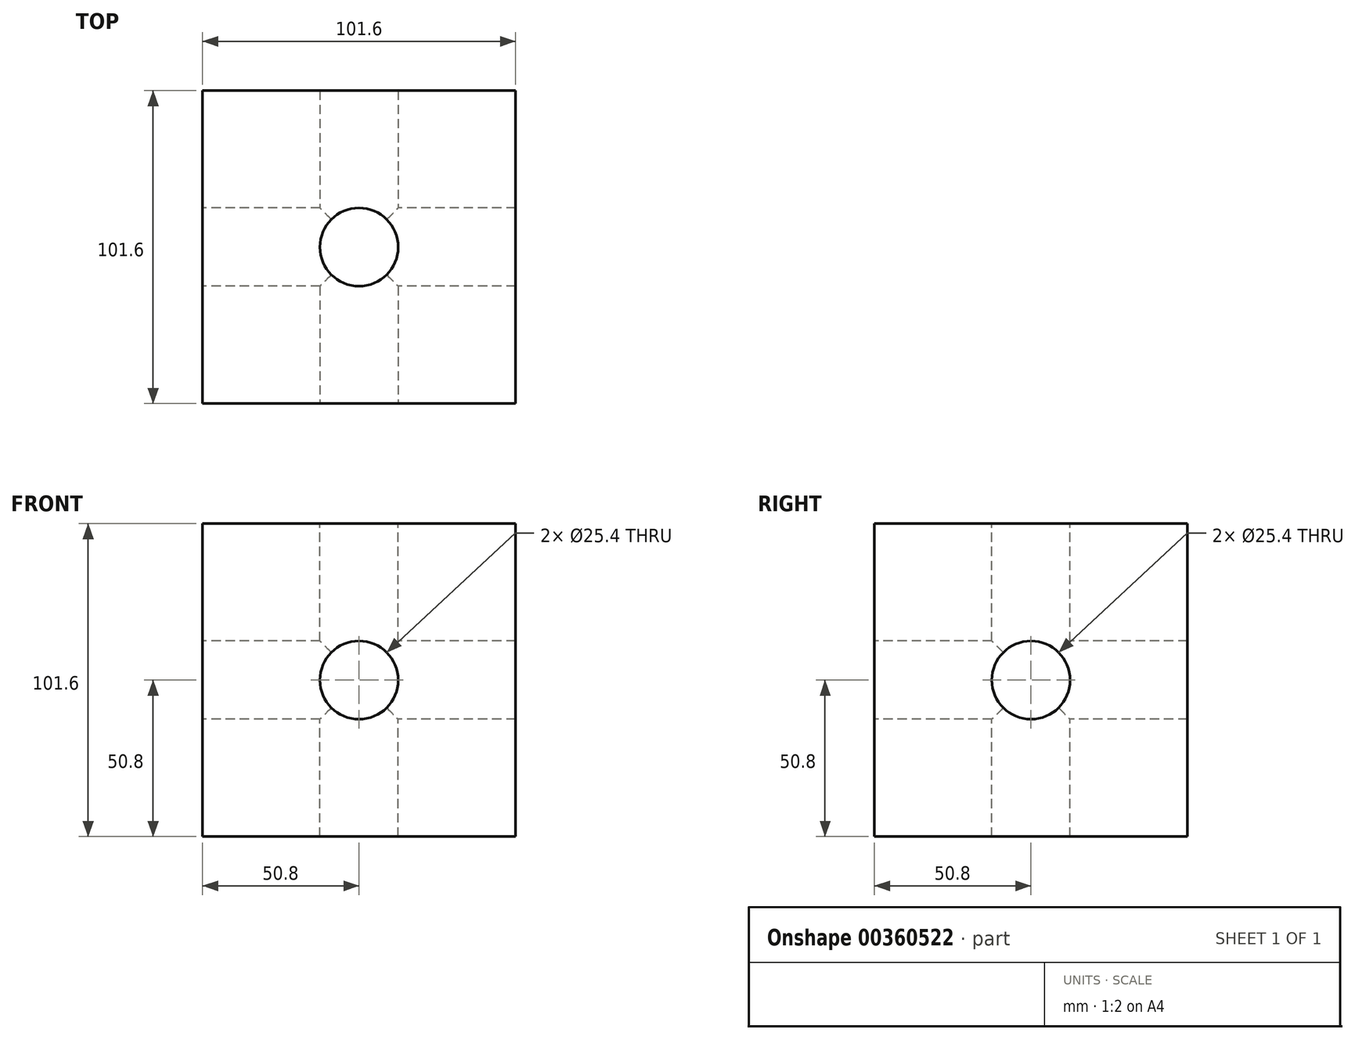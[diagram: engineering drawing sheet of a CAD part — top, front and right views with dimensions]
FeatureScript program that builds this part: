
annotation { "Feature Type Name" : "Feature", "Feature Type Description" : "" }
export const myFeature = defineFeature(function(context is Context, id is Id, definition is map)
    precondition{}
    {
        {
            var Q0;
            Q0=qCreatedBy(makeId("Front.planeOp"),FACE);
            var sketch = newSketch(context, id + "F0", { "sketchPlane" : qUnion([Q0])});
            skLineSegment(sketch, "E0.bottom", {"start": v(0, 0) * mm, "end": v(-50.8, 0) * mm});
            skLineSegment(sketch, "E0.top", {"start": v(0, 50.8) * mm, "end": v(-50.8, 50.8) * mm});
            skLineSegment(sketch, "E0.left", {"start": v(0, 0) * mm, "end": v(0, 50.8) * mm});
            skLineSegment(sketch, "E0.right", {"start": v(-50.8, 0) * mm, "end": v(-50.8, 50.8) * mm});
            skSolve(sketch);
        }
        {
            var Q0;
            Q0 = qSketchRegion(id + "F0", true);
            extrude(context, id + "F1", {"entities" : qUnion([Q0]), "depth" : 50.8 * mm});
        }
        {
            var Q0;
            Q0=qCreatedBy(makeId("Front.planeOp"),FACE);
            var sketch = newSketch(context, id + "F2", { "sketchPlane" : qUnion([Q0])});
            skLineSegment(sketch, "E1.bottom", {"start": v(25.4, -25.4) * mm, "end": v(-76.2, -25.4) * mm});
            skLineSegment(sketch, "E1.top", {"start": v(25.4, 76.2) * mm, "end": v(-76.2, 76.2) * mm});
            skLineSegment(sketch, "E1.left", {"start": v(25.4, -25.4) * mm, "end": v(25.4, 76.2) * mm});
            skLineSegment(sketch, "E1.right", {"start": v(-76.2, -25.4) * mm, "end": v(-76.2, 76.2) * mm});
            skSolve(sketch);
        }
        {
            var Q0;
            Q0=makeQuery(id+"F2.imprint","IMPRINT",FACE,{"disambiguationData":[TD([[makeQuery(id+"F2.imprint","IMPRINT",EDGE,{"derivedFrom":sQuery(id+"F2.wireOp",EDGE,"E1.bottom")}),-1.0]])]});
            extrude(context, id + "F3", {"entities" : qUnion([Q0]), "operationType" : NewBodyOperationType.ADD, "depth" : 76.2 * mm});
        }
        {
            var Q0;
            Q0=makeQuery(id+"F3.boolean.opBoolean","MERGE",FACE,{"derivedFrom":[makeQuery(id+"F1.opExtrude","CAP_FACE",FACE,{"disambiguationData":[OSD([sQuery(id+"F0.wireOp",EDGE,"E0.bottom"),sQuery(id+"F0.wireOp",EDGE,"E0.top"),sQuery(id+"F0.wireOp",EDGE,"E0.left"),sQuery(id+"F0.wireOp",EDGE,"E0.right")])],"isStart":true}),makeQuery(id+"F3.opExtrude","CAP_FACE",FACE,{"disambiguationData":[OSD([sQuery(id+"F2.wireOp",EDGE,"E1.bottom"),sQuery(id+"F2.wireOp",EDGE,"E1.top"),sQuery(id+"F2.wireOp",EDGE,"E1.left"),sQuery(id+"F2.wireOp",EDGE,"E1.right")])],"isStart":true})]});
            extrude(context, id + "F4", {"entities" : qUnion([Q0]), "operationType" : NewBodyOperationType.ADD, "depth" : 25.4 * mm});
        }
        {
            var Q0;
            {var subQ0=sQuery(id+"F2.wireOp",EDGE,"E1.top");Q0=makeQuery(id+"F4.boolean.opBoolean","MERGE",FACE,{"derivedFrom":[makeQuery(id+"F3.opExtrude","SWEPT_FACE",FACE,{"disambiguationData":[OSD([subQ0])]}),makeQuery(id+"F4.opExtrude","SWEPT_FACE",FACE,{"disambiguationData":[OSD([subQ0])]})]});}
            var sketch = newSketch(context, id + "F5", { "sketchPlane" : qUnion([Q0])});
            skCircle(sketch, "E2", {"center": v(-25.4, -25.4) * mm, "radius": 18.47 * mm});
            skSolve(sketch);
        }
        {
            var Q0;
            Q0=sQuery(id+"F5.wireOp",VERTEX,"E2.center");
            var Q1;
            Q1=makeQuery(id+"F1.opExtrude","SWEPT_BODY",BODY,{"disambiguationData":[OSD([sQuery(id+"F0.wireOp",EDGE,"E0.bottom"),sQuery(id+"F0.wireOp",EDGE,"E0.top"),sQuery(id+"F0.wireOp",EDGE,"E0.left"),sQuery(id+"F0.wireOp",EDGE,"E0.right")])]});
            hole(context, id + "F6", {"style" : HoleStyle.SIMPLE, "endStyle" : HoleEndStyle.THROUGH, "holeDiameter" : 25.4 * mm, "isTappedThrough" : true, "tappedDepth" : 12.7 * mm, "tapClearance" : 3, "locations" : qUnion([Q0]), "scope" : qUnion([Q1])});
        }
        {
            var Q0;
            {var subQ0=sQuery(id+"F2.wireOp",EDGE,"E1.right");Q0=makeQuery(id+"F4.boolean.opBoolean","MERGE",FACE,{"derivedFrom":[makeQuery(id+"F3.opExtrude","SWEPT_FACE",FACE,{"disambiguationData":[OSD([subQ0])]}),makeQuery(id+"F4.opExtrude","SWEPT_FACE",FACE,{"disambiguationData":[OSD([subQ0])]})]});}
            var sketch = newSketch(context, id + "F7", { "sketchPlane" : qUnion([Q0])});
            skPoint(sketch, "E3", {"position": v(25.4, 25.4) * mm});
            skSolve(sketch);
        }
        {
            var Q0;
            Q0=sQuery(id+"F7.wireOp",VERTEX,"E3");
            var Q1;
            Q1=makeQuery(id+"F1.opExtrude","SWEPT_BODY",BODY,{"disambiguationData":[OSD([sQuery(id+"F0.wireOp",EDGE,"E0.bottom"),sQuery(id+"F0.wireOp",EDGE,"E0.top"),sQuery(id+"F0.wireOp",EDGE,"E0.left"),sQuery(id+"F0.wireOp",EDGE,"E0.right")])]});
            hole(context, id + "F8", {"style" : HoleStyle.SIMPLE, "endStyle" : HoleEndStyle.THROUGH, "holeDiameter" : 25.4 * mm, "isTappedThrough" : true, "tappedDepth" : 12.7 * mm, "tapClearance" : 3, "locations" : qUnion([Q0]), "scope" : qUnion([Q1])});
        }
        {
            var Q0;
            Q0=makeQuery(id+"F3.opExtrude","CAP_FACE",FACE,{"disambiguationData":[OSD([sQuery(id+"F2.wireOp",EDGE,"E1.bottom"),sQuery(id+"F2.wireOp",EDGE,"E1.top"),sQuery(id+"F2.wireOp",EDGE,"E1.left"),sQuery(id+"F2.wireOp",EDGE,"E1.right")])],"isStart":false});
            var sketch = newSketch(context, id + "F9", { "sketchPlane" : qUnion([Q0])});
            skPoint(sketch, "E4", {"position": v(-25.4, 25.4) * mm});
            skSolve(sketch);
        }
        {
            var Q0;
            Q0=sQuery(id+"F9.wireOp",VERTEX,"E4");
            var Q1;
            Q1=makeQuery(id+"F1.opExtrude","SWEPT_BODY",BODY,{"disambiguationData":[OSD([sQuery(id+"F0.wireOp",EDGE,"E0.bottom"),sQuery(id+"F0.wireOp",EDGE,"E0.top"),sQuery(id+"F0.wireOp",EDGE,"E0.left"),sQuery(id+"F0.wireOp",EDGE,"E0.right")])]});
            hole(context, id + "F10", {"style" : HoleStyle.SIMPLE, "endStyle" : HoleEndStyle.THROUGH, "holeDiameter" : 25.4 * mm, "isTappedThrough" : true, "tappedDepth" : 12.7 * mm, "tapClearance" : 3, "locations" : qUnion([Q0]), "scope" : qUnion([Q1])});
        }
    });
